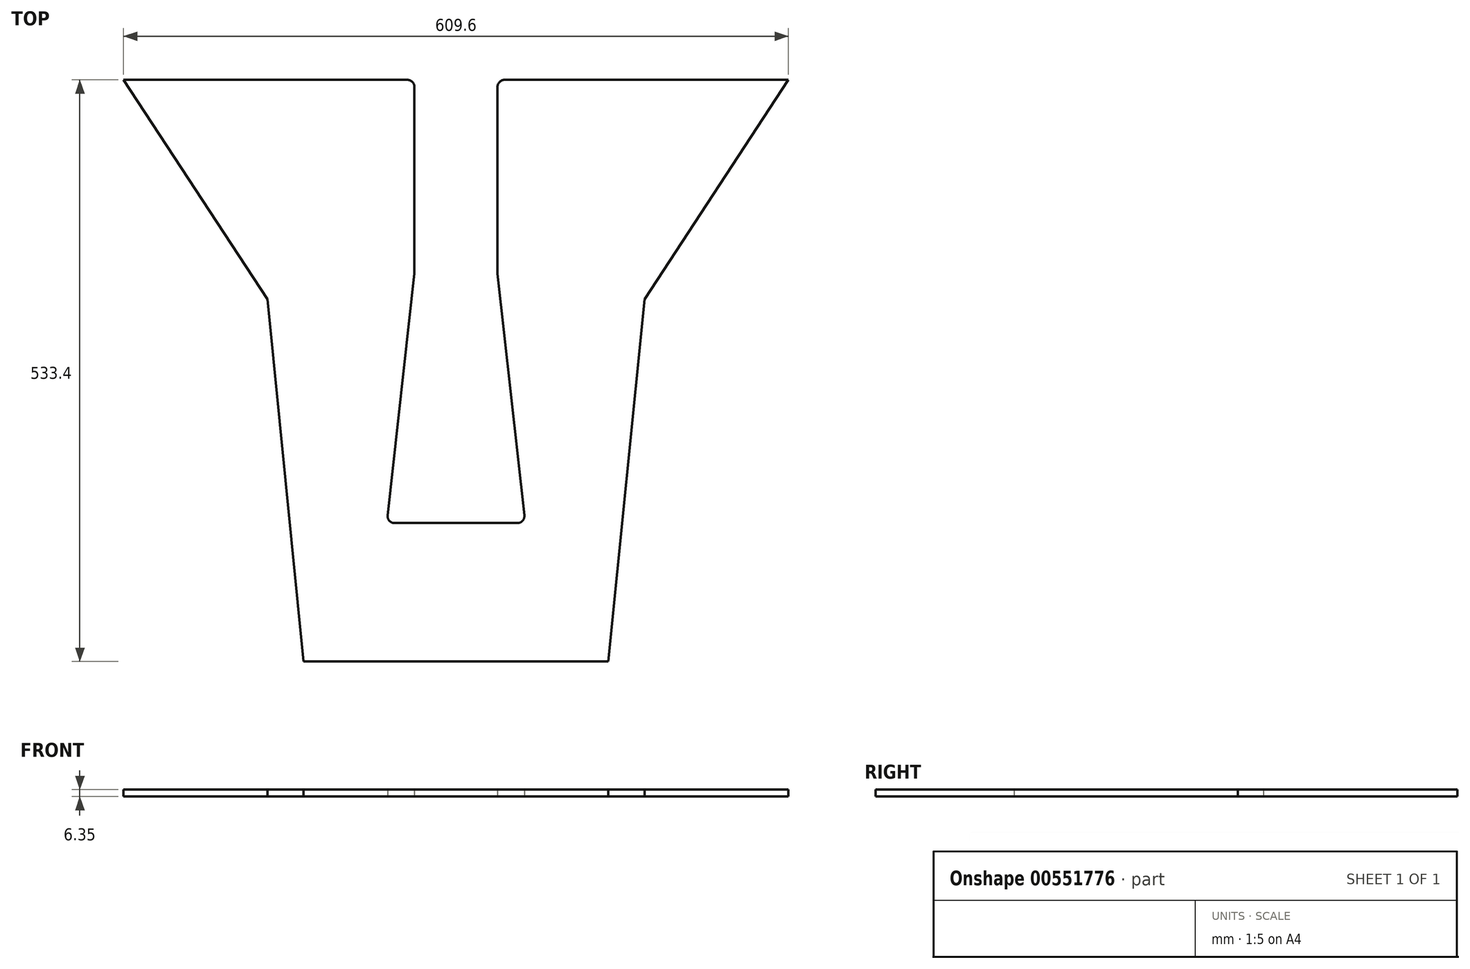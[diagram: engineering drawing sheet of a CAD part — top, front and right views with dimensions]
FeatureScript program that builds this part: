
annotation { "Feature Type Name" : "Feature", "Feature Type Description" : "" }
export const myFeature = defineFeature(function(context is Context, id is Id, definition is map)
    precondition{}
    {
        {
            var Q0;
            Q0=qCreatedBy(makeId("Top.planeOp"),FACE);
            var sketch = newSketch(context, id + "F0", { "sketchPlane" : qUnion([Q0])});
            skLineSegment(sketch, "E0", {"start": v(0, 0) * mm, "end": v(-139.7, 0) * mm});
            skLineSegment(sketch, "E1", {"start": v(0, 0) * mm, "end": v(139.7, 0) * mm});
            skLineSegment(sketch, "E2", {"start": v(0, 0) * mm, "end": v(0, 514.35) * mm, "construction": true});
            skPoint(sketch, "E3", {"position": v(0, 304.8) * mm});
            skPoint(sketch, "E4", {"position": v(0, 381) * mm});
            skLineSegment(sketch, "E5", {"start": v(0, 381) * mm, "end": v(-883.72, 381) * mm, "construction": true});
            skLineSegment(sketch, "E6", {"start": v(0, 381) * mm, "end": v(761.76, 381) * mm, "construction": true});
            skPoint(sketch, "E7", {"position": v(-177.8, 381) * mm});
            skPoint(sketch, "E8", {"position": v(209.55, 381) * mm});
            skPoint(sketch, "E9", {"position": v(177.8, 381) * mm});
            skPoint(sketch, "E10", {"position": v(-172.92, 332.15) * mm});
            skPoint(sketch, "E11", {"position": v(172.92, 332.15) * mm});
            skLineSegment(sketch, "E12", {"start": v(172.92, 332.15) * mm, "end": v(139.7, 0) * mm});
            skLineSegment(sketch, "E13", {"start": v(-172.92, 332.15) * mm, "end": v(-139.7, 0) * mm, "construction": true});
            skLineSegment(sketch, "E14", {"start": v(-172.92, 332.15) * mm, "end": v(-139.7, 0) * mm});
            skPoint(sketch, "E15", {"position": v(0, 127) * mm});
            skPoint(sketch, "E16", {"position": v(-63.5, 127) * mm});
            skPoint(sketch, "E17", {"position": v(63.5, 127) * mm});
            skLineSegment(sketch, "E18", {"start": v(-56.4, 127) * mm, "end": v(0, 127) * mm});
            skLineSegment(sketch, "E19", {"start": v(56.4, 127) * mm, "end": v(0, 127) * mm});
            skPoint(sketch, "E20", {"position": v(0, 355.6) * mm});
            skLineSegment(sketch, "E21", {"start": v(0, 355.6) * mm, "end": v(-38.1, 355.6) * mm, "construction": true});
            skLineSegment(sketch, "E22", {"start": v(0, 355.6) * mm, "end": v(38.1, 355.6) * mm, "construction": true});
            skLineSegment(sketch, "E23", {"start": v(-62.72, 134.05) * mm, "end": v(-38.1, 355.6) * mm});
            skLineSegment(sketch, "E24", {"start": v(62.72, 134.05) * mm, "end": v(38.1, 355.6) * mm});
            skArc(sketch, "E25.filletArc", {"start": v(-62.72, 134.05) * mm, "mid": v(-61.14, 129.12) * mm, "end": v(-56.4, 127) * mm});
            skArc(sketch, "E26.filletArc", {"start": v(56.4, 127) * mm, "mid": v(61.14, 129.12) * mm, "end": v(62.72, 134.05) * mm});
            skPoint(sketch, "E27", {"position": v(0, 514.35) * mm});
            skLineSegment(sketch, "E28", {"start": v(-44.45, 533.4) * mm, "end": v(-304.8, 533.4) * mm});
            skLineSegment(sketch, "E29", {"start": v(44.45, 533.4) * mm, "end": v(304.8, 533.4) * mm});
            skLineSegment(sketch, "E30", {"start": v(-172.92, 332.15) * mm, "end": v(-304.8, 533.4) * mm});
            skLineSegment(sketch, "E31", {"start": v(172.92, 332.15) * mm, "end": v(304.8, 533.4) * mm});
            skLineSegment(sketch, "E32", {"start": v(-38.1, 355.6) * mm, "end": v(-38.1, 527.05) * mm});
            skLineSegment(sketch, "E33", {"start": v(38.1, 355.6) * mm, "end": v(38.1, 527.05) * mm});
            skArc(sketch, "E34.filletArc", {"start": v(-38.1, 527.05) * mm, "mid": v(-39.96, 531.54) * mm, "end": v(-44.45, 533.4) * mm});
            skArc(sketch, "E35.filletArc", {"start": v(44.45, 533.4) * mm, "mid": v(39.96, 531.54) * mm, "end": v(38.1, 527.05) * mm});
            skSolve(sketch);
        }
        {
            var Q0;
            Q0=makeQuery(id+"F0.imprint","IMPRINT",FACE,{"disambiguationData":[TD([[makeQuery(id+"F0.imprint","IMPRINT",EDGE,{"derivedFrom":sQuery(id+"F0.wireOp",EDGE,"E0")}),-1.0]])]});
            extrude(context, id + "F1", {"entities" : qUnion([Q0]), "depth" : 6.35 * mm, "offsetDistance" : 25.4 * mm});
        }
    });
